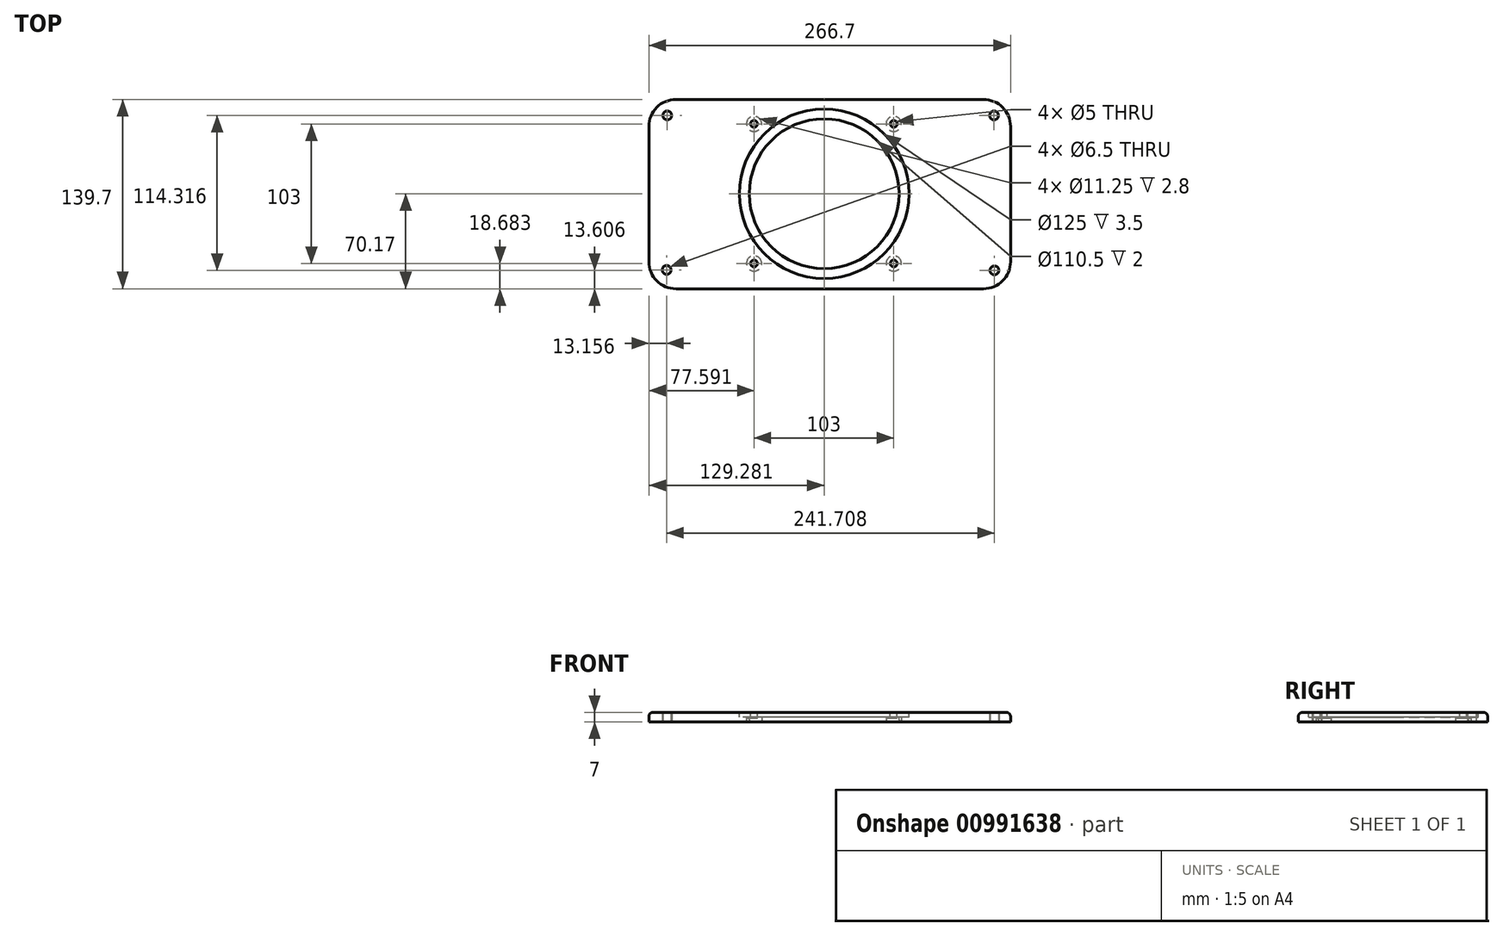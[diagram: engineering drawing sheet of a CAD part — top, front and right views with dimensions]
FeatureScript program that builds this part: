
annotation { "Feature Type Name" : "Feature", "Feature Type Description" : "" }
export const myFeature = defineFeature(function(context is Context, id is Id, definition is map)
    precondition{}
    {
        {
            var Q0;
            Q0=qCreatedBy(makeId("Top.planeOp"),FACE);
            var sketch = newSketch(context, id + "F0", { "sketchPlane" : qUnion([Q0])});
            skLineSegment(sketch, "E0.bottom", {"start": v(-62.7, 69.53) * mm, "end": v(204, 69.53) * mm});
            skLineSegment(sketch, "E0.top", {"start": v(-62.7, -70.17) * mm, "end": v(204, -70.17) * mm});
            skLineSegment(sketch, "E0.left", {"start": v(-62.7, 69.53) * mm, "end": v(-62.7, -70.17) * mm});
            skLineSegment(sketch, "E0.right", {"start": v(204, 69.53) * mm, "end": v(204, -70.17) * mm});
            skSolve(sketch);
        }
        {
            var Q0;
            Q0 = qSketchRegion(id + "F0", true);
            extrude(context, id + "F1", {"entities" : qUnion([Q0]), "depth" : 7 * mm, "offsetDistance" : 25 * mm});
        }
        {
            var Q0;
            Q0=makeQuery(id+"F1.opExtrude","SWEPT_EDGE",EDGE,{"disambiguationData":[OSD([sQuery(id+"F0.wireOp",EDGE,"E0.bottom"),sQuery(id+"F0.wireOp",EDGE,"E0.left")])]});
            var Q1;
            Q1=makeQuery(id+"F1.opExtrude","SWEPT_EDGE",EDGE,{"disambiguationData":[OSD([sQuery(id+"F0.wireOp",EDGE,"E0.bottom"),sQuery(id+"F0.wireOp",EDGE,"E0.right")])]});
            var Q2;
            Q2=makeQuery(id+"F1.opExtrude","SWEPT_EDGE",EDGE,{"disambiguationData":[OSD([sQuery(id+"F0.wireOp",EDGE,"E0.top"),sQuery(id+"F0.wireOp",EDGE,"E0.left")])]});
            var Q3;
            Q3=makeQuery(id+"F1.opExtrude","SWEPT_EDGE",EDGE,{"disambiguationData":[OSD([sQuery(id+"F0.wireOp",EDGE,"E0.top"),sQuery(id+"F0.wireOp",EDGE,"E0.right")])]});
            fillet(context, id + "F2", {"entities" : qUnion([Q0, Q1, Q2, Q3]), "radius" : 20 * mm, "tangentPropagation" : true, "allowEdgeOverflow" : false});
        }
        {
            var Q0;
            Q0=makeQuery(id+"F1.opExtrude","CAP_FACE",FACE,{"disambiguationData":[OSD([sQuery(id+"F0.wireOp",EDGE,"E0.bottom"),sQuery(id+"F0.wireOp",EDGE,"E0.top"),sQuery(id+"F0.wireOp",EDGE,"E0.left"),sQuery(id+"F0.wireOp",EDGE,"E0.right")])],"isStart":false});
            var sketch = newSketch(context, id + "F3", { "sketchPlane" : qUnion([Q0])});
            skCircle(sketch, "E1", {"center": v(66.58, 0) * mm, "radius": 62.5 * mm});
            skCircle(sketch, "E2", {"center": v(66.58, 0) * mm, "radius": 55.25 * mm});
            skSolve(sketch);
        }
        {
            var Q0;
            Q0 = qSketchRegion(id + "F3", true);
            extrude(context, id + "F4", {"entities" : qUnion([Q0]), "operationType" : NewBodyOperationType.REMOVE, "oppositeDirection" : true, "depth" : 3.5 * mm, "offsetDistance" : 25 * mm});
        }
        {
            var Q0;
            Q0=makeQuery(id+"F3.imprint","IMPRINT",FACE,{"disambiguationData":[TD([[makeQuery(id+"F3.imprint","IMPRINT",EDGE,{"derivedFrom":sQuery(id+"F3.wireOp",EDGE,"E2")}),1.0]])]});
            extrude(context, id + "F5", {"entities" : qUnion([Q0]), "operationType" : NewBodyOperationType.REMOVE, "oppositeDirection" : true, "depth" : 10 * mm, "offsetDistance" : 25 * mm});
        }
        {
            var Q0;
            Q0=makeQuery(id+"F1.opExtrude","CAP_FACE",FACE,{"disambiguationData":[OSD([sQuery(id+"F0.wireOp",EDGE,"E0.bottom"),sQuery(id+"F0.wireOp",EDGE,"E0.top"),sQuery(id+"F0.wireOp",EDGE,"E0.left"),sQuery(id+"F0.wireOp",EDGE,"E0.right")])],"isStart":true});
            var sketch = newSketch(context, id + "F6", { "sketchPlane" : qUnion([Q0])});
            skCircle(sketch, "E3", {"center": v(-49.54, 56.21) * mm, "radius": 3.25 * mm});
            skCircle(sketch, "E4", {"center": v(192.16, 56.56) * mm, "radius": 3.25 * mm});
            skCircle(sketch, "E5", {"center": v(191.88, -57.75) * mm, "radius": 3.25 * mm});
            skCircle(sketch, "E6", {"center": v(-49.09, -57.75) * mm, "radius": 3.25 * mm});
            skSolve(sketch);
        }
        {
            var Q0;
            Q0=makeQuery(id+"F6.imprint","IMPRINT",FACE,{"disambiguationData":[TD([[makeQuery(id+"F6.imprint","IMPRINT",EDGE,{"derivedFrom":sQuery(id+"F6.wireOp",EDGE,"E3")}),1.0]])]});
            var Q1;
            Q1=makeQuery(id+"F6.imprint","IMPRINT",FACE,{"disambiguationData":[TD([[makeQuery(id+"F6.imprint","IMPRINT",EDGE,{"derivedFrom":sQuery(id+"F6.wireOp",EDGE,"E4")}),1.0]])]});
            var Q2;
            Q2=makeQuery(id+"F6.imprint","IMPRINT",FACE,{"disambiguationData":[TD([[makeQuery(id+"F6.imprint","IMPRINT",EDGE,{"derivedFrom":sQuery(id+"F6.wireOp",EDGE,"E5")}),1.0]])]});
            var Q3;
            Q3=makeQuery(id+"F6.imprint","IMPRINT",FACE,{"disambiguationData":[TD([[makeQuery(id+"F6.imprint","IMPRINT",EDGE,{"derivedFrom":sQuery(id+"F6.wireOp",EDGE,"E6")}),1.0]])]});
            extrude(context, id + "F7", {"entities" : qUnion([Q0, Q1, Q2, Q3]), "operationType" : NewBodyOperationType.REMOVE, "oppositeDirection" : true, "depth" : 8 * mm, "offsetDistance" : 25 * mm});
        }
        {
            var Q0;
            {var subQ0=sQuery(id+"F0.wireOp",EDGE,"E0.left");var subQ1=sQuery(id+"F0.wireOp",EDGE,"E0.bottom");var subQ2=sQuery(id+"F0.wireOp",EDGE,"E0.top");var subQ3=sQuery(id+"F0.wireOp",EDGE,"E0.right");Q0=makeQuery(id+"F4.boolean.opBoolean","SPLIT",FACE,{"disambiguationData":[TD([makeQuery(id+"F1.opExtrude","SWEPT_FACE",FACE,{"disambiguationData":[OSD([subQ1])]})])],"derivedFrom":makeQuery(id+"F1.opExtrude","CAP_FACE",FACE,{"disambiguationData":[OSD([subQ1,subQ2,subQ0,subQ3])],"isStart":false})});}
            var sketch = newSketch(context, id + "F8", { "sketchPlane" : qUnion([Q0])});
            skCircle(sketch, "E7", {"center": v(14.9, 51.51) * mm, "radius": 2.5 * mm});
            skCircle(sketch, "E8", {"center": v(117.9, 51.51) * mm, "radius": 2.5 * mm});
            skCircle(sketch, "E9", {"center": v(117.9, -51.49) * mm, "radius": 2.5 * mm});
            skCircle(sketch, "E10", {"center": v(14.9, -51.49) * mm, "radius": 2.5 * mm});
            skSolve(sketch);
        }
        {
            var Q0;
            Q0 = qSketchRegion(id + "F8", true);
            extrude(context, id + "F9", {"entities" : qUnion([Q0]), "operationType" : NewBodyOperationType.REMOVE, "oppositeDirection" : true, "depth" : 8 * mm, "offsetDistance" : 25 * mm});
        }
        {
            var Q0;
            Q0=makeQuery(id+"F1.opExtrude","CAP_FACE",FACE,{"disambiguationData":[OSD([sQuery(id+"F0.wireOp",EDGE,"E0.bottom"),sQuery(id+"F0.wireOp",EDGE,"E0.top"),sQuery(id+"F0.wireOp",EDGE,"E0.left"),sQuery(id+"F0.wireOp",EDGE,"E0.right")])],"isStart":true});
            var sketch = newSketch(context, id + "F10", { "sketchPlane" : qUnion([Q0])});
            skCircle(sketch, "E11", {"center": v(14.9, 51.49) * mm, "radius": 5.62 * mm});
            skCircle(sketch, "E12", {"center": v(117.9, 51.49) * mm, "radius": 5.62 * mm});
            skCircle(sketch, "E13", {"center": v(117.9, -51.51) * mm, "radius": 5.62 * mm});
            skCircle(sketch, "E14", {"center": v(14.9, -51.51) * mm, "radius": 5.62 * mm});
            skSolve(sketch);
        }
        {
            var Q0;
            Q0 = qSketchRegion(id + "F10", true);
            extrude(context, id + "F11", {"entities" : qUnion([Q0]), "operationType" : NewBodyOperationType.REMOVE, "oppositeDirection" : true, "depth" : 2.8 * mm, "offsetDistance" : 25 * mm});
        }
        {
            var Q0;
            Q0=makeQuery(id+"F5.boolean.opBoolean","INTERSECT",EDGE,{"derivedFrom":[makeQuery(id+"F1.opExtrude","CAP_FACE",FACE,{"disambiguationData":[OSD([sQuery(id+"F0.wireOp",EDGE,"E0.bottom"),sQuery(id+"F0.wireOp",EDGE,"E0.top"),sQuery(id+"F0.wireOp",EDGE,"E0.left"),sQuery(id+"F0.wireOp",EDGE,"E0.right")])],"isStart":true}),makeQuery(id+"F5.opExtrude","SWEPT_FACE",FACE,{"disambiguationData":[OSD([sQuery(id+"F3.wireOp",EDGE,"E2")])]})]});
            fillet(context, id + "F12", {"entities" : qUnion([Q0]), "radius" : 1.5 * mm, "tangentPropagation" : true, "allowEdgeOverflow" : false});
        }
        {
            var Q0;
            Q0=makeQuery(id+"F1.opExtrude","CAP_EDGE",EDGE,{"disambiguationData":[OSD([sQuery(id+"F0.wireOp",EDGE,"E0.bottom")])],"isStart":false});
            fillet(context, id + "F13", {"entities" : qUnion([Q0]), "radius" : 3 * mm, "tangentPropagation" : true, "allowEdgeOverflow" : false});
        }
    });
